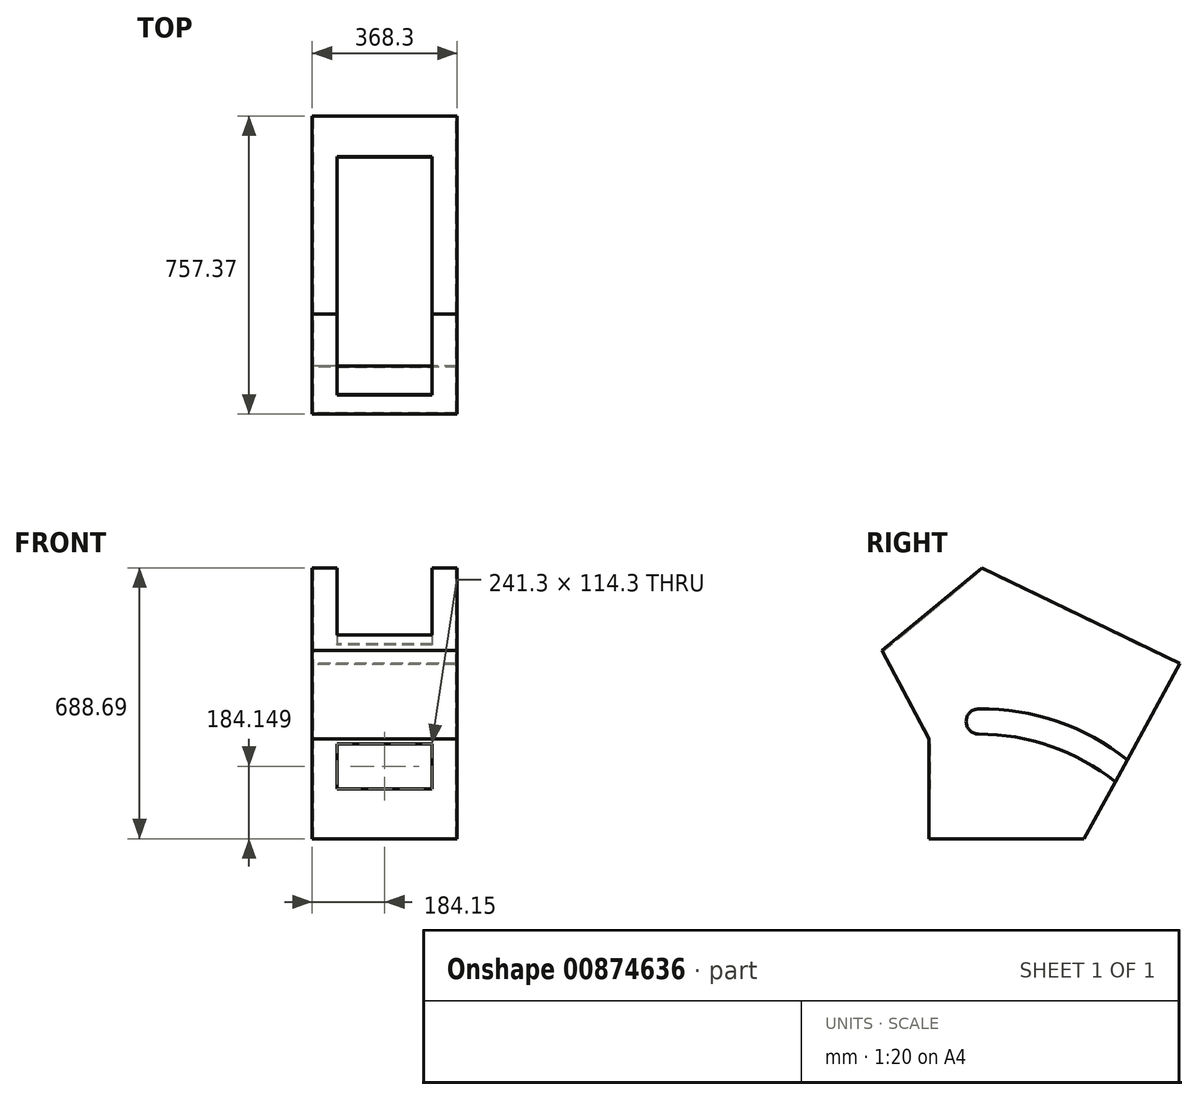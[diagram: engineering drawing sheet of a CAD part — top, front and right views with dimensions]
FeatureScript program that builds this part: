
annotation { "Feature Type Name" : "Feature", "Feature Type Description" : "" }
export const myFeature = defineFeature(function(context is Context, id is Id, definition is map)
    precondition{}
    {
        {
            var Q0;
            Q0=qCreatedBy(makeId("Right.planeOp"),FACE);
            var sketch = newSketch(context, id + "F0", { "sketchPlane" : qUnion([Q0])});
            skLineSegment(sketch, "E0", {"start": v(169.3, -219.58) * mm, "end": v(-224.4, -219.58) * mm});
            skLineSegment(sketch, "E1", {"start": v(-224.4, -219.58) * mm, "end": v(-224.4, 34.42) * mm});
            skLineSegment(sketch, "E2", {"start": v(-224.4, 34.42) * mm, "end": v(-344.27, 258.36) * mm});
            skLineSegment(sketch, "E3", {"start": v(-344.27, 258.36) * mm, "end": v(-90.08, 469.11) * mm});
            skLineSegment(sketch, "E4", {"start": v(-90.08, 469.11) * mm, "end": v(413.1, 226.09) * mm});
            skLineSegment(sketch, "E5", {"start": v(413.1, 226.09) * mm, "end": v(169.3, -219.58) * mm});
            skSolve(sketch);
        }
        {
            var Q0;
            Q0 = qSketchRegion(id + "F0", true);
            extrude(context, id + "F1", {"entities" : qUnion([Q0]), "depth" : 368.3 * mm, "offsetDistance" : 25.4 * mm});
        }
        {
            var Q0;
            Q0=makeQuery(id+"F1.opExtrude","SWEPT_FACE",FACE,{"disambiguationData":[OSD([sQuery(id+"F0.wireOp",EDGE,"E5")])]});
            var Q1;
            Q1=makeQuery(id+"F1.opExtrude","SWEPT_FACE",FACE,{"disambiguationData":[OSD([sQuery(id+"F0.wireOp",EDGE,"E0")])]});
            shell(context, id + "F2", {"entities" : qUnion([Q0, Q1]), "thickness" : 2.54 * mm});
        }
        {
            var Q0;
            Q0=makeQuery(id+"F1.opExtrude","SWEPT_FACE",FACE,{"disambiguationData":[OSD([sQuery(id+"F0.wireOp",EDGE,"E4")])]});
            var sketch = newSketch(context, id + "F3", { "sketchPlane" : qUnion([Q0])});
            skLineSegment(sketch, "E6.bottom", {"start": v(304.8, -285.14) * mm, "end": v(63.5, -285.14) * mm});
            skLineSegment(sketch, "E6.top", {"start": v(304.8, 159.36) * mm, "end": v(63.5, 159.36) * mm});
            skLineSegment(sketch, "E6.left", {"start": v(304.8, -285.14) * mm, "end": v(304.8, 159.36) * mm});
            skLineSegment(sketch, "E6.right", {"start": v(63.5, -285.14) * mm, "end": v(63.5, 159.36) * mm});
            skSolve(sketch);
        }
        {
            var Q0;
            Q0 = qSketchRegion(id + "F3", true);
            extrude(context, id + "F4", {"entities" : qUnion([Q0]), "operationType" : NewBodyOperationType.REMOVE, "oppositeDirection" : true, "depth" : 25.4 * mm, "offsetDistance" : 25.4 * mm});
        }
        {
            var Q0;
            Q0=makeQuery(id+"F1.opExtrude","SWEPT_FACE",FACE,{"disambiguationData":[OSD([sQuery(id+"F0.wireOp",EDGE,"E3")])]});
            var sketch = newSketch(context, id + "F5", { "sketchPlane" : qUnion([Q0])});
            skLineSegment(sketch, "E7.bottom", {"start": v(63.5, 230.07) * mm, "end": v(304.8, 230.07) * mm});
            skLineSegment(sketch, "E7.top", {"start": v(63.5, -36.63) * mm, "end": v(304.8, -36.63) * mm});
            skLineSegment(sketch, "E7.left", {"start": v(63.5, 230.07) * mm, "end": v(63.5, -36.63) * mm});
            skLineSegment(sketch, "E7.right", {"start": v(304.8, 230.07) * mm, "end": v(304.8, -36.63) * mm});
            skSolve(sketch);
        }
        {
            var Q0;
            Q0 = qSketchRegion(id + "F5", true);
            extrude(context, id + "F6", {"entities" : qUnion([Q0]), "operationType" : NewBodyOperationType.REMOVE, "oppositeDirection" : true, "depth" : 25.4 * mm, "offsetDistance" : 25.4 * mm});
        }
        {
            var Q0;
            Q0=makeQuery(id+"F1.opExtrude","SWEPT_FACE",FACE,{"disambiguationData":[OSD([sQuery(id+"F0.wireOp",EDGE,"E1")])]});
            var sketch = newSketch(context, id + "F7", { "sketchPlane" : qUnion([Q0])});
            skLineSegment(sketch, "E8.bottom", {"start": v(63.5, 21.72) * mm, "end": v(304.8, 21.72) * mm});
            skLineSegment(sketch, "E8.top", {"start": v(63.5, -92.58) * mm, "end": v(304.8, -92.58) * mm});
            skLineSegment(sketch, "E8.left", {"start": v(63.5, 21.72) * mm, "end": v(63.5, -92.58) * mm});
            skLineSegment(sketch, "E8.right", {"start": v(304.8, 21.72) * mm, "end": v(304.8, -92.58) * mm});
            skSolve(sketch);
        }
        {
            var Q0;
            Q0 = qSketchRegion(id + "F7", true);
            extrude(context, id + "F8", {"entities" : qUnion([Q0]), "operationType" : NewBodyOperationType.REMOVE, "oppositeDirection" : true, "depth" : 25.4 * mm, "offsetDistance" : 25.4 * mm});
        }
        {
            var Q0;
            Q0=makeQuery(id+"F1.opExtrude","CAP_FACE",FACE,{"disambiguationData":[OSD([sQuery(id+"F0.wireOp",EDGE,"E0"),sQuery(id+"F0.wireOp",EDGE,"E1"),sQuery(id+"F0.wireOp",EDGE,"E2"),sQuery(id+"F0.wireOp",EDGE,"E3"),sQuery(id+"F0.wireOp",EDGE,"E4"),sQuery(id+"F0.wireOp",EDGE,"E5")])],"isStart":false});
            var sketch = newSketch(context, id + "F9", { "sketchPlane" : qUnion([Q0])});
            skLineSegment(sketch, "E9", {"start": v(-224.4, 34.42) * mm, "end": v(-95.64, 34.42) * mm, "construction": true});
            skLineSegment(sketch, "E10", {"start": v(-95.64, 34.42) * mm, "end": v(58.05, 34.42) * mm, "construction": true});
            skLineSegment(sketch, "E11", {"start": v(-224.4, -219.58) * mm, "end": v(-98.61, -219.58) * mm});
            skLineSegment(sketch, "E12", {"start": v(-98.61, -219.58) * mm, "end": v(54.15, -219.58) * mm});
            skLineSegment(sketch, "E13", {"start": v(169.3, -219.58) * mm, "end": v(248.53, -74.74) * mm, "construction": true});
            skArc(sketch, "E14", {"start": v(248.53, -74.74) * mm, "mid": v(85.28, 15.47) * mm, "end": v(-98.61, 46.6) * mm});
            skArc(sketch, "E15", {"start": v(-98.61, 110.1) * mm, "mid": v(-130.36, 78.36) * mm, "end": v(-98.61, 46.6) * mm});
            skArc(sketch, "E16", {"start": v(279, -19.03) * mm, "mid": v(101.52, 78.63) * mm, "end": v(-98.61, 110.1) * mm});
            skSolve(sketch);
        }
        {
            var Q0;
            Q0 = qSketchRegion(id + "F9", true);
            var Q1;
            {var subQ0=sQuery(id+"F9.wireOp",EDGE,"E14");Q1=makeQuery(id+"F9.imprint","IMPRINT",FACE,{"disambiguationData":[TD([[makeQuery(id+"F9.imprint","IMPRINT",EDGE,{"derivedFrom":subQ0}),-1.0]])]});}
            extrude(context, id + "F10", {"entities" : qUnion([Q0, Q1]), "operationType" : NewBodyOperationType.REMOVE, "oppositeDirection" : true, "depth" : 25.4 * mm, "offsetDistance" : 25.4 * mm});
        }
    });
